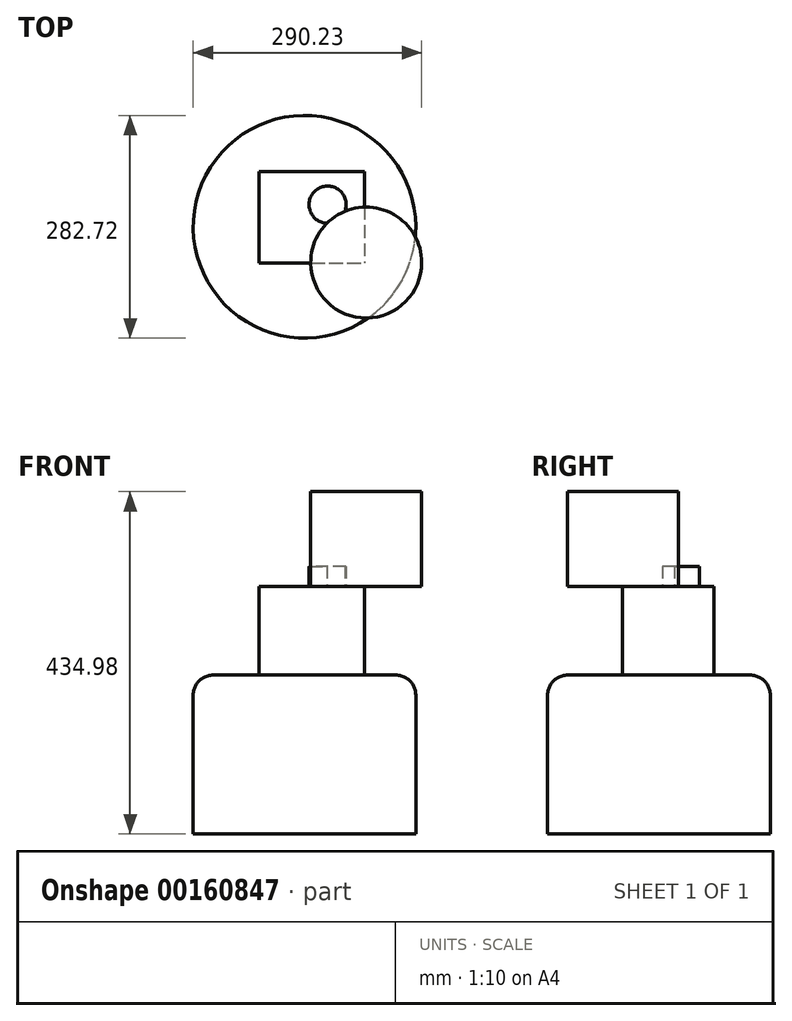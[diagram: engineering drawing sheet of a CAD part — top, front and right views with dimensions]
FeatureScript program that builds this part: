
annotation { "Feature Type Name" : "Feature", "Feature Type Description" : "" }
export const myFeature = defineFeature(function(context is Context, id is Id, definition is map)
    precondition{}
    {
        {
            var Q0;
            Q0=qCreatedBy(makeId("Top.planeOp"),FACE);
            var sketch = newSketch(context, id + "F0", { "sketchPlane" : qUnion([Q0])});
            skCircle(sketch, "E0", {"center": v(0, 0) * mm, "radius": 141.36 * mm});
            skSolve(sketch);
        }
        {
            var Q0;
            Q0 = qSketchRegion(id + "F0", true);
            extrude(context, id + "F1", {"entities" : qUnion([Q0]), "depth" : 201.93 * mm});
        }
        {
            var Q0;
            Q0=makeQuery(id+"F1.opExtrude","CAP_FACE",FACE,{"disambiguationData":[OSD([sQuery(id+"F0.wireOp",EDGE,"E0")])],"isStart":false});
            var sketch = newSketch(context, id + "F2", { "sketchPlane" : qUnion([Q0])});
            skSolve(sketch);
        }
        {
            var Q0;
            Q0=makeQuery(id+"F2.imprint","IMPRINT",FACE,{"disambiguationData":[TD([[makeQuery(id+"F2.imprint","IMPRINT",EDGE,{"derivedFrom":makeQuery(id+"F1.opExtrude","CAP_EDGE",EDGE,{"disambiguationData":[OSD([sQuery(id+"F0.wireOp",EDGE,"E0")])],"isStart":false})}),1.0]])]});
            var sketch = newSketch(context, id + "F3", { "sketchPlane" : qUnion([Q0])});
            skLineSegment(sketch, "E1.bottom", {"start": v(-57.93, 69.9) * mm, "end": v(76.11, 69.9) * mm});
            skLineSegment(sketch, "E1.top", {"start": v(-57.93, -46.24) * mm, "end": v(76.11, -46.24) * mm});
            skLineSegment(sketch, "E1.left", {"start": v(-57.93, 69.9) * mm, "end": v(-57.93, -46.24) * mm});
            skLineSegment(sketch, "E1.right", {"start": v(76.11, 69.9) * mm, "end": v(76.11, -46.24) * mm});
            skSolve(sketch);
        }
        {
            var Q0;
            Q0 = qSketchRegion(id + "F3", true);
            extrude(context, id + "F4", {"entities" : qUnion([Q0]), "operationType" : NewBodyOperationType.ADD, "depth" : 112.4 * mm});
        }
        {
            var Q0;
            Q0=makeQuery(id+"F1.opExtrude","CAP_EDGE",EDGE,{"disambiguationData":[OSD([sQuery(id+"F0.wireOp",EDGE,"E0")])],"isStart":false});
            fillet(context, id + "F5", {"entities" : qUnion([Q0]), "radius" : 25.4 * mm, "tangentPropagation" : true, "allowEdgeOverflow" : false});
        }
        {
            var Q0;
            Q0=makeQuery(id+"F4.opExtrude","CAP_FACE",FACE,{"disambiguationData":[OSD([sQuery(id+"F3.wireOp",EDGE,"E1.bottom"),sQuery(id+"F3.wireOp",EDGE,"E1.top"),sQuery(id+"F3.wireOp",EDGE,"E1.left"),sQuery(id+"F3.wireOp",EDGE,"E1.right")])],"isStart":false});
            var sketch = newSketch(context, id + "F6", { "sketchPlane" : qUnion([Q0])});
            skLineSegment(sketch, "E2", {"start": v(-57.93, -46.24) * mm, "end": v(76.11, 69.9) * mm});
            skLineSegment(sketch, "E3", {"start": v(76.11, 69.9) * mm, "end": v(76.11, -46.24) * mm});
            skLineSegment(sketch, "E4", {"start": v(76.11, -46.24) * mm, "end": v(-57.93, -46.24) * mm});
            skSolve(sketch);
        }
        {
            var Q0;
            Q0=makeQuery(id+"F6.imprint","IMPRINT",FACE,{"disambiguationData":[TD([[makeQuery(id+"F6.imprint","IMPRINT",EDGE,{"derivedFrom":sQuery(id+"F6.wireOp",EDGE,"E2")}),-1.0]])]});
            var sketch = newSketch(context, id + "F7", { "sketchPlane" : qUnion([Q0])});
            skCircle(sketch, "E5", {"center": v(29.33, 28.16) * mm, "radius": 23.56 * mm});
            skSolve(sketch);
        }
        {
            var Q0;
            Q0 = qSketchRegion(id + "F7", true);
            extrude(context, id + "F8", {"entities" : qUnion([Q0]), "operationType" : NewBodyOperationType.ADD, "depth" : 25.4 * mm});
        }
        {
            var Q0;
            Q0=makeQuery(id+"F6.imprint","IMPRINT",FACE,{"disambiguationData":[TD([[makeQuery(id+"F6.imprint","IMPRINT",EDGE,{"derivedFrom":sQuery(id+"F6.wireOp",EDGE,"E2")}),-1.0]])]});
            var sketch = newSketch(context, id + "F9", { "sketchPlane" : qUnion([Q0])});
            skCircle(sketch, "E6", {"center": v(78.4, -45.44) * mm, "radius": 70.48 * mm});
            skSolve(sketch);
        }
        {
            var Q0;
            Q0 = qSketchRegion(id + "F9", true);
            extrude(context, id + "F10", {"entities" : qUnion([Q0]), "operationType" : NewBodyOperationType.ADD, "depth" : 120.65 * mm, "offsetDistance" : 25.4 * mm});
        }
    });
